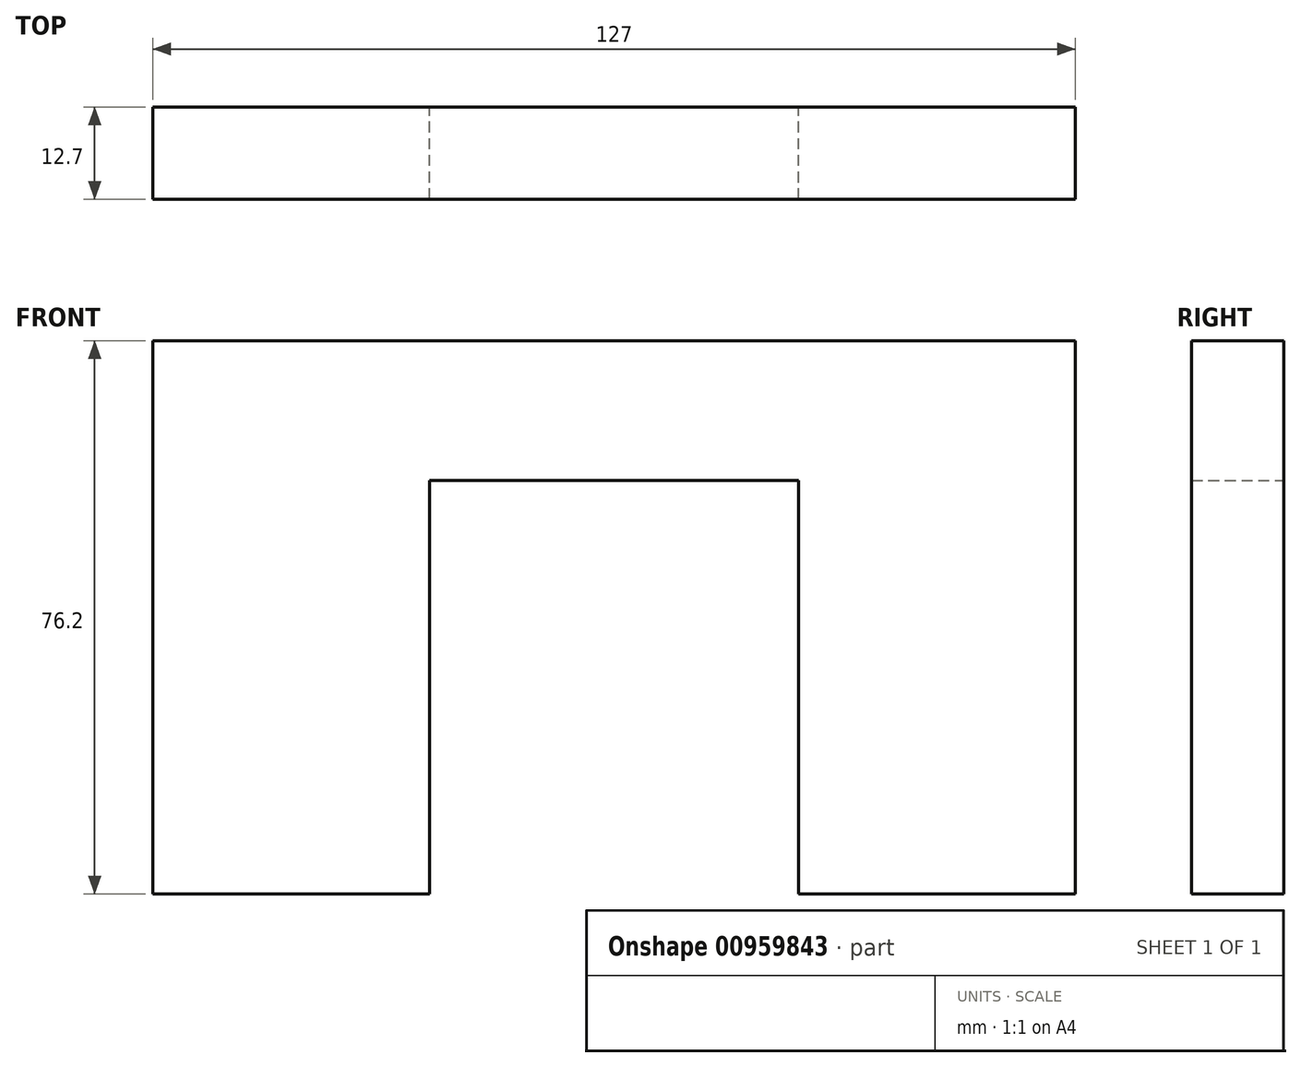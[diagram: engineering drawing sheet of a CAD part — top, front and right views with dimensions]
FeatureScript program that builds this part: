
annotation { "Feature Type Name" : "Feature", "Feature Type Description" : "" }
export const myFeature = defineFeature(function(context is Context, id is Id, definition is map)
    precondition{}
    {
        {
            var Q0;
            Q0=qCreatedBy(makeId("Front.planeOp"),FACE);
            var sketch = newSketch(context, id + "F0", { "sketchPlane" : qUnion([Q0])});
            skLineSegment(sketch, "E0", {"start": v(-38.28, -37.39) * mm, "end": v(-38.28, 38.81) * mm});
            skLineSegment(sketch, "E1", {"start": v(-38.28, 38.81) * mm, "end": v(88.72, 38.81) * mm});
            skLineSegment(sketch, "E2", {"start": v(88.72, 38.81) * mm, "end": v(88.72, -37.39) * mm});
            skLineSegment(sketch, "E3", {"start": v(-0.18, -37.39) * mm, "end": v(-0.18, 19.58) * mm});
            skLineSegment(sketch, "E4", {"start": v(-0.18, 19.58) * mm, "end": v(50.62, 19.58) * mm});
            skLineSegment(sketch, "E5", {"start": v(50.62, 19.58) * mm, "end": v(50.62, -37.39) * mm});
            skLineSegment(sketch, "E6", {"start": v(-38.28, -37.39) * mm, "end": v(-0.18, -37.39) * mm});
            skLineSegment(sketch, "E7", {"start": v(50.62, -37.39) * mm, "end": v(88.72, -37.39) * mm});
            skSolve(sketch);
        }
        {
            var Q0;
            Q0 = qSketchRegion(id + "F0", true);
            extrude(context, id + "F1", {"entities" : qUnion([Q0]), "endBound" : BoundingType.SYMMETRIC, "depth" : 12.7 * mm, "offsetDistance" : 25.4 * mm});
        }
    });
